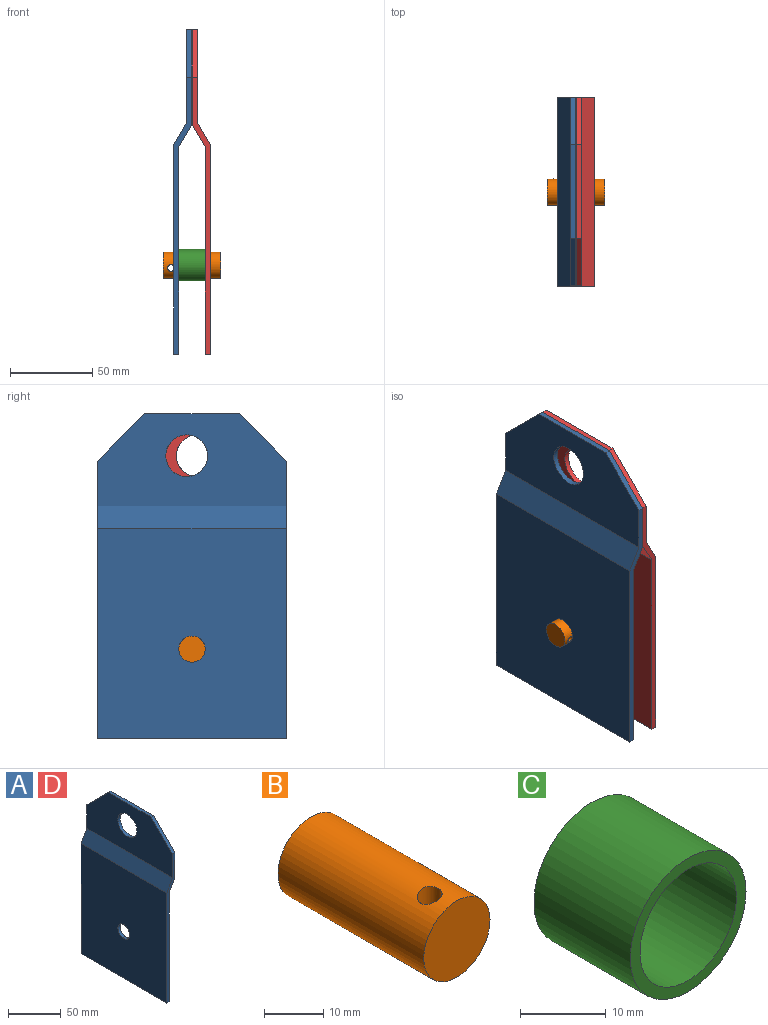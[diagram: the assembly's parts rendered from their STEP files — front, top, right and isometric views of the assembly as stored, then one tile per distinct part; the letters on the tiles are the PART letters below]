
ASSEMBLY  parts=4 mates=3
PART A: 14 faces, bbox 11.1x114.3x196.6 mm
  f0: plane 114.3x55.87mm, normal (-1,0,0), area 5063.1mm2, adj f2,f3,f8,f9,f11,f12,f13
  f1: plane 114.3x57.15mm, normal (1,0,0), area 5209mm2, adj f2,f7,f8,f9,f11,f12,f13
  f2: plane 57.15x3.18mm, normal (0,0,1), area 181.5mm2, adj f0,f1,f12,f13
  f3: plane 114.3x13.75mm, normal (-0.87,0,0.5), area 1814.5mm2, adj f0,f4,f8,f9
  f4: plane 127x114.3mm, normal (-1,0,0), area 14318.2mm2, adj f3,f5,f8,f9,f10
  f5: plane 114.3x3.18mm, normal (0,0,-1), area 362.9mm2, adj f4,f6,f8,f9
  f6: plane 125.72x114.3mm, normal (1,0,0), area 14172.3mm2, adj f5,f7,f8,f9,f10
  f7: plane 114.3x13.75mm, normal (0.87,0,-0.5), area 1814.5mm2, adj f1,f6,f8,f9
  f8: plane 168.05x11.11mm, normal (0,-1,0), area 543.7mm2, adj f0,f1,f3,f4,f5,f6,f7,f13
  f9: plane 168.05x11.11mm, normal (0,1,0), area 543.7mm2, adj f0,f1,f3,f4,f5,f6,f7,f12
  f10: cylinder r=7.94mm len=15.88mm, axis (1,0,0), area 158.3mm2, adj f4,f6
  f11: cylinder r=12.7mm len=25.4mm, axis (-1,0,0), area 253.4mm2, adj f0,f1
  f12: plane 28.58x28.58mm, normal (0,0.71,0.71), area 128.3mm2, adj f0,f1,f2,f9
  f13: plane 28.58x28.58mm, normal (0,-0.71,0.71), area 128.3mm2, adj f0,f1,f2,f8
PART B: 4 faces, bbox 15.9x34.9x15.9 mm
  f0: cylinder r=7.94mm len=34.93mm, axis (0,1,0), area 1713.3mm2, adj f1,f2,f3
  f1: plane 15.88x15.88mm, normal (0,-1,0), area 197.9mm2, adj f0
  f2: plane 15.88x15.88mm, normal (0,1,0), area 197.9mm2, adj f0
  f3: cylinder r=2.09mm len=15.88mm, axis (0,0,-1), area 199.7mm2, adj f0
PART C: 4 faces, bbox 19.1x15.9x19.1 mm
  f0: cylinder r=7.94mm len=15.88mm, axis (0,1,0), area 791.7mm2, adj f2,f3
  f1: cylinder r=9.53mm len=19.05mm, axis (0,1,0), area 950.1mm2, adj f2,f3
  f2: plane 19.05x19.05mm, normal (0,-1,0), area 87.1mm2, adj f0,f1
  f3: plane 19.05x19.05mm, normal (0,1,0), area 87.1mm2, adj f0,f1
PART D: same geometry as A
PLACE A t=(-31.06,17.52,29.38)mm
PLACE B rot(axis=(-0.58,-0.58,-0.58),120deg) t=(-10.42,-49.99,-37.68)mm
PLACE C rot(axis=(0.58,0.58,-0.58),120deg) t=(-19.95,-32.77,-55.2)mm
PLACE D rot(axis=(0,0,-1),180deg) t=(-24.71,-96.78,29.38)mm
MATE revolute C.f0 <-> A.f10  axis (-1,0,0) through (-35.82,-39.63,-45.56)mm
MATE revolute D.f10 <-> C.f0  axis (-1,0,0) through (-19.95,-39.63,-45.56)mm
MATE fastened B.f0 <-> A.f10  axis (-1,0,0) through (-45.35,-39.63,-45.56)mm
